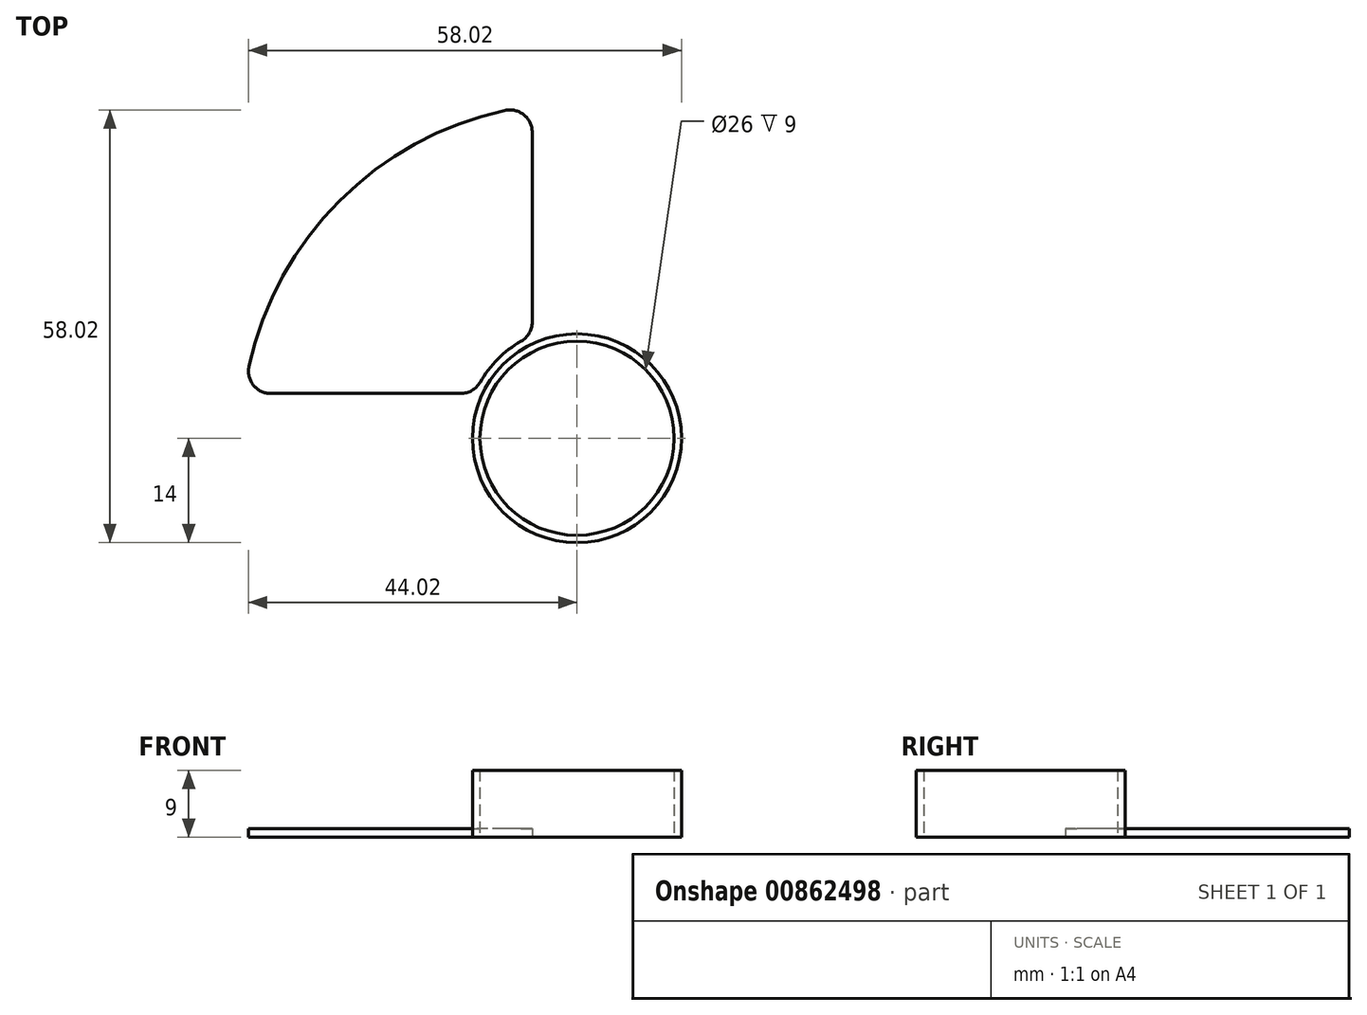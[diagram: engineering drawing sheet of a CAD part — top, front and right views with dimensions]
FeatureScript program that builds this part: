
annotation { "Feature Type Name" : "Feature", "Feature Type Description" : "" }
export const myFeature = defineFeature(function(context is Context, id is Id, definition is map)
    precondition{}
    {
        {
            var Q0;
            Q0=qCreatedBy(makeId("Top.planeOp"),FACE);
            var sketch = newSketch(context, id + "F0", { "sketchPlane" : qUnion([Q0])});
            skArc(sketch, "E0", {"start": v(-13, 7.5) * mm, "mid": v(-10.6, 10.6) * mm, "end": v(-7.5, 13) * mm});
            skArc(sketch, "E1", {"start": v(-55, 0) * mm, "mid": v(-38.9, 38.9) * mm, "end": v(0, 55) * mm});
            skLineSegment(sketch, "E2", {"start": v(-6, 15.59) * mm, "end": v(-6, 41.02) * mm});
            skLineSegment(sketch, "E3", {"start": v(-15.59, 6) * mm, "end": v(-41.02, 6) * mm});
            skArc(sketch, "E4", {"start": v(-43.95, 9.64) * mm, "mid": v(-31.82, 31.82) * mm, "end": v(-9.64, 43.95) * mm});
            skPoint(sketch, "E5.orphan", {"position": v(0, 6) * mm});
            skPoint(sketch, "E6.orphan", {"position": v(-6, 0) * mm});
            skPoint(sketch, "E7.orphan", {"position": v(0, 45) * mm});
            skPoint(sketch, "E8.orphan", {"position": v(-45, 0) * mm});
            skPoint(sketch, "E9.orphan", {"position": v(-15, 0) * mm});
            skPoint(sketch, "E10.orphan", {"position": v(0, 15) * mm});
            skPoint(sketch, "E11.visualSharp", {"position": v(-44.6, 6) * mm});
            skArc(sketch, "E11.filletArc", {"start": v(-43.95, 9.64) * mm, "mid": v(-43.36, 7.12) * mm, "end": v(-41.02, 6) * mm});
            skPoint(sketch, "E12.visualSharp", {"position": v(-6, 44.6) * mm});
            skArc(sketch, "E12.filletArc", {"start": v(-6, 41.02) * mm, "mid": v(-7.12, 43.36) * mm, "end": v(-9.64, 43.95) * mm});
            skPoint(sketch, "E13.visualSharp", {"position": v(-6, 13.75) * mm});
            skArc(sketch, "E13.filletArc", {"start": v(-7.5, 13) * mm, "mid": v(-6.4, 14.09) * mm, "end": v(-6, 15.59) * mm});
            skPoint(sketch, "E14.visualSharp", {"position": v(-13.75, 6) * mm});
            skArc(sketch, "E14.filletArc", {"start": v(-15.59, 6) * mm, "mid": v(-14.09, 6.4) * mm, "end": v(-13, 7.5) * mm});
            skArc(sketch, "E15.1.0", {"start": v(0, -55) * mm, "mid": v(-38.9, -38.9) * mm, "end": v(-55, 0) * mm});
            skArc(sketch, "E15.1.1", {"start": v(-9.64, -43.95) * mm, "mid": v(-31.82, -31.82) * mm, "end": v(-43.95, -9.64) * mm});
            skArc(sketch, "E15.1.2", {"start": v(-41.02, -6) * mm, "mid": v(-43.36, -7.12) * mm, "end": v(-43.95, -9.64) * mm});
            skLineSegment(sketch, "E15.1.3", {"start": v(-15.59, -6) * mm, "end": v(-41.02, -6) * mm});
            skArc(sketch, "E15.1.4", {"start": v(-13, -7.5) * mm, "mid": v(-14.09, -6.4) * mm, "end": v(-15.59, -6) * mm});
            skArc(sketch, "E15.1.5", {"start": v(-7.5, -13) * mm, "mid": v(-10.6, -10.6) * mm, "end": v(-13, -7.5) * mm});
            skArc(sketch, "E15.1.6", {"start": v(-6, -15.59) * mm, "mid": v(-6.4, -14.09) * mm, "end": v(-7.5, -13) * mm});
            skLineSegment(sketch, "E15.1.7", {"start": v(-6, -15.59) * mm, "end": v(-6, -41.02) * mm});
            skArc(sketch, "E15.1.8", {"start": v(-9.64, -43.95) * mm, "mid": v(-7.12, -43.36) * mm, "end": v(-6, -41.02) * mm});
            skArc(sketch, "E15.2.0", {"start": v(55, 0) * mm, "mid": v(38.9, -38.9) * mm, "end": v(0, -55) * mm});
            skArc(sketch, "E15.2.1", {"start": v(43.95, -9.64) * mm, "mid": v(31.82, -31.82) * mm, "end": v(9.64, -43.95) * mm});
            skArc(sketch, "E15.2.2", {"start": v(6, -41.02) * mm, "mid": v(7.12, -43.36) * mm, "end": v(9.64, -43.95) * mm});
            skLineSegment(sketch, "E15.2.3", {"start": v(6, -15.59) * mm, "end": v(6, -41.02) * mm});
            skArc(sketch, "E15.2.4", {"start": v(7.5, -13) * mm, "mid": v(6.4, -14.09) * mm, "end": v(6, -15.59) * mm});
            skArc(sketch, "E15.2.5", {"start": v(13, -7.5) * mm, "mid": v(10.6, -10.6) * mm, "end": v(7.5, -13) * mm});
            skArc(sketch, "E15.2.6", {"start": v(15.59, -6) * mm, "mid": v(14.09, -6.4) * mm, "end": v(13, -7.5) * mm});
            skLineSegment(sketch, "E15.2.7", {"start": v(15.59, -6) * mm, "end": v(41.02, -6) * mm});
            skArc(sketch, "E15.2.8", {"start": v(43.95, -9.64) * mm, "mid": v(43.36, -7.12) * mm, "end": v(41.02, -6) * mm});
            skArc(sketch, "E15.3.0", {"start": v(0, 55) * mm, "mid": v(38.9, 38.9) * mm, "end": v(55, 0) * mm});
            skArc(sketch, "E15.3.1", {"start": v(9.64, 43.95) * mm, "mid": v(31.82, 31.82) * mm, "end": v(43.95, 9.64) * mm});
            skArc(sketch, "E15.3.2", {"start": v(41.02, 6) * mm, "mid": v(43.36, 7.12) * mm, "end": v(43.95, 9.64) * mm});
            skLineSegment(sketch, "E15.3.3", {"start": v(15.59, 6) * mm, "end": v(41.02, 6) * mm});
            skArc(sketch, "E15.3.4", {"start": v(13, 7.5) * mm, "mid": v(14.09, 6.4) * mm, "end": v(15.59, 6) * mm});
            skArc(sketch, "E15.3.5", {"start": v(7.5, 13) * mm, "mid": v(10.6, 10.6) * mm, "end": v(13, 7.5) * mm});
            skArc(sketch, "E15.3.6", {"start": v(6, 15.59) * mm, "mid": v(6.4, 14.09) * mm, "end": v(7.5, 13) * mm});
            skLineSegment(sketch, "E15.3.7", {"start": v(6, 15.59) * mm, "end": v(6, 41.02) * mm});
            skArc(sketch, "E15.3.8", {"start": v(9.64, 43.95) * mm, "mid": v(7.12, 43.36) * mm, "end": v(6, 41.02) * mm});
            skSolve(sketch);
        }
        {
            var Q0;
            Q0=makeQuery(id+"F0.imprint","IMPRINT",FACE,{"disambiguationData":[TD([[makeQuery(id+"F0.imprint","IMPRINT",EDGE,{"derivedFrom":sQuery(id+"F0.wireOp",EDGE,"E0")}),-1.0]])]});
            extrude(context, id + "F1", {"entities" : qUnion([Q0]), "depth" : 1.2 * mm, "offsetDistance" : 25 * mm});
        }
        {
            var Q0;
            Q0=qCreatedBy(makeId("Top.planeOp"),FACE);
            var sketch = newSketch(context, id + "F2", { "sketchPlane" : qUnion([Q0])});
            skCircle(sketch, "E16", {"center": v(0, 0) * mm, "radius": 14 * mm});
            skCircle(sketch, "E17", {"center": v(0, 0) * mm, "radius": 13 * mm});
            skSolve(sketch);
        }
        {
            var Q0;
            Q0=makeQuery(id+"F2.imprint","IMPRINT",FACE,{"disambiguationData":[TD([[makeQuery(id+"F2.imprint","IMPRINT",EDGE,{"derivedFrom":sQuery(id+"F2.wireOp",EDGE,"E16")}),1.0]])]});
            extrude(context, id + "F3", {"entities" : qUnion([Q0]), "operationType" : NewBodyOperationType.ADD, "depth" : 9 * mm, "offsetDistance" : 25 * mm});
        }
        {
            var Q0;
            Q0=qCreatedBy(makeId("Top.planeOp"),FACE);
            var sketch = newSketch(context, id + "F4", { "sketchPlane" : qUnion([Q0])});
            skLineSegment(sketch, "E18", {"start": v(0, 0) * mm, "end": v(-15.01, -8.67) * mm, "construction": true});
            skArc(sketch, "E19", {"start": v(-5.63, -3.25) * mm, "mid": v(-5.63, 3.25) * mm, "end": v(0, 6.5) * mm});
            skLineSegment(sketch, "E20", {"start": v(-8.6, -3.52) * mm, "end": v(-6.15, -2.1) * mm});
            skArc(sketch, "E21", {"start": v(-8.6, -3.52) * mm, "mid": v(-9.21, -4.28) * mm, "end": v(-9.1, -5.25) * mm});
            skLineSegment(sketch, "E22", {"start": v(0, 0) * mm, "end": v(-10.91, 6.3) * mm, "construction": true});
            skLineSegment(sketch, "E23.MirrorCS", {"start": v(-1.25, 9.2) * mm, "end": v(-1.25, 6.38) * mm});
            skArc(sketch, "E24.MirrorCS", {"start": v(-1.25, 9.2) * mm, "mid": v(-0.9, 10.12) * mm, "end": v(0, 10.5) * mm});
            skArc(sketch, "E25.1.0", {"start": v(5.63, -3.25) * mm, "mid": v(0, -6.5) * mm, "end": v(-5.63, -3.25) * mm});
            skLineSegment(sketch, "E25.1.1", {"start": v(7.34, -5.68) * mm, "end": v(4.9, -4.27) * mm});
            skArc(sketch, "E25.1.2", {"start": v(7.34, -5.68) * mm, "mid": v(8.3, -5.84) * mm, "end": v(9.1, -5.25) * mm});
            skLineSegment(sketch, "E25.1.3", {"start": v(-7.34, -5.68) * mm, "end": v(-4.9, -4.27) * mm});
            skArc(sketch, "E25.1.4", {"start": v(-7.34, -5.68) * mm, "mid": v(-8.3, -5.84) * mm, "end": v(-9.1, -5.25) * mm});
            skArc(sketch, "E25.2.0", {"start": v(0, 6.5) * mm, "mid": v(5.63, 3.25) * mm, "end": v(5.63, -3.25) * mm});
            skLineSegment(sketch, "E25.2.1", {"start": v(1.25, 9.2) * mm, "end": v(1.25, 6.38) * mm});
            skArc(sketch, "E25.2.2", {"start": v(1.25, 9.2) * mm, "mid": v(0.9, 10.12) * mm, "end": v(0, 10.5) * mm});
            skLineSegment(sketch, "E25.2.3", {"start": v(8.6, -3.52) * mm, "end": v(6.15, -2.1) * mm});
            skArc(sketch, "E25.2.4", {"start": v(8.6, -3.52) * mm, "mid": v(9.21, -4.28) * mm, "end": v(9.1, -5.25) * mm});
            skSolve(sketch);
        }
        {
            var Q0;
            {var subQ1=sQuery(id+"F4.wireOp",EDGE,"E25.1.0");var subQ4=sQuery(id+"F4.wireOp",EDGE,"E19");var subQ8=makeQuery(id+"F4.imprint","INTERSECT",VERTEX,{"derivedFrom":[subQ4,subQ1]});Q0=makeQuery(id+"F4.imprint","IMPRINT",FACE,{"disambiguationData":[TD([[makeQuery(id+"F4.imprint","IMPRINT",EDGE,{"disambiguationData":[TD([[subQ8,-1.0]])],"derivedFrom":subQ4}),-1.0]])]});}
            var Q1;
            {var subQ4=sQuery(id+"F4.wireOp",EDGE,"E20");Q1=makeQuery(id+"F4.imprint","IMPRINT",FACE,{"disambiguationData":[TD([[makeQuery(id+"F4.imprint","IMPRINT",EDGE,{"derivedFrom":subQ4}),-1.0]])]});}
            var Q2;
            {var subQ4=sQuery(id+"F4.wireOp",EDGE,"E25.1.1");Q2=makeQuery(id+"F4.imprint","IMPRINT",FACE,{"disambiguationData":[TD([[makeQuery(id+"F4.imprint","IMPRINT",EDGE,{"derivedFrom":subQ4}),-1.0]])]});}
            var Q3;
            {var subQ4=sQuery(id+"F4.wireOp",EDGE,"E23.MirrorCS");Q3=makeQuery(id+"F4.imprint","IMPRINT",FACE,{"disambiguationData":[TD([[makeQuery(id+"F4.imprint","IMPRINT",EDGE,{"derivedFrom":subQ4}),1.0]])]});}
            extrude(context, id + "F5", {"entities" : qUnion([Q0, Q1, Q2, Q3]), "operationType" : NewBodyOperationType.REMOVE, "depth" : 25 * mm, "offsetDistance" : 25 * mm});
        }
    });
